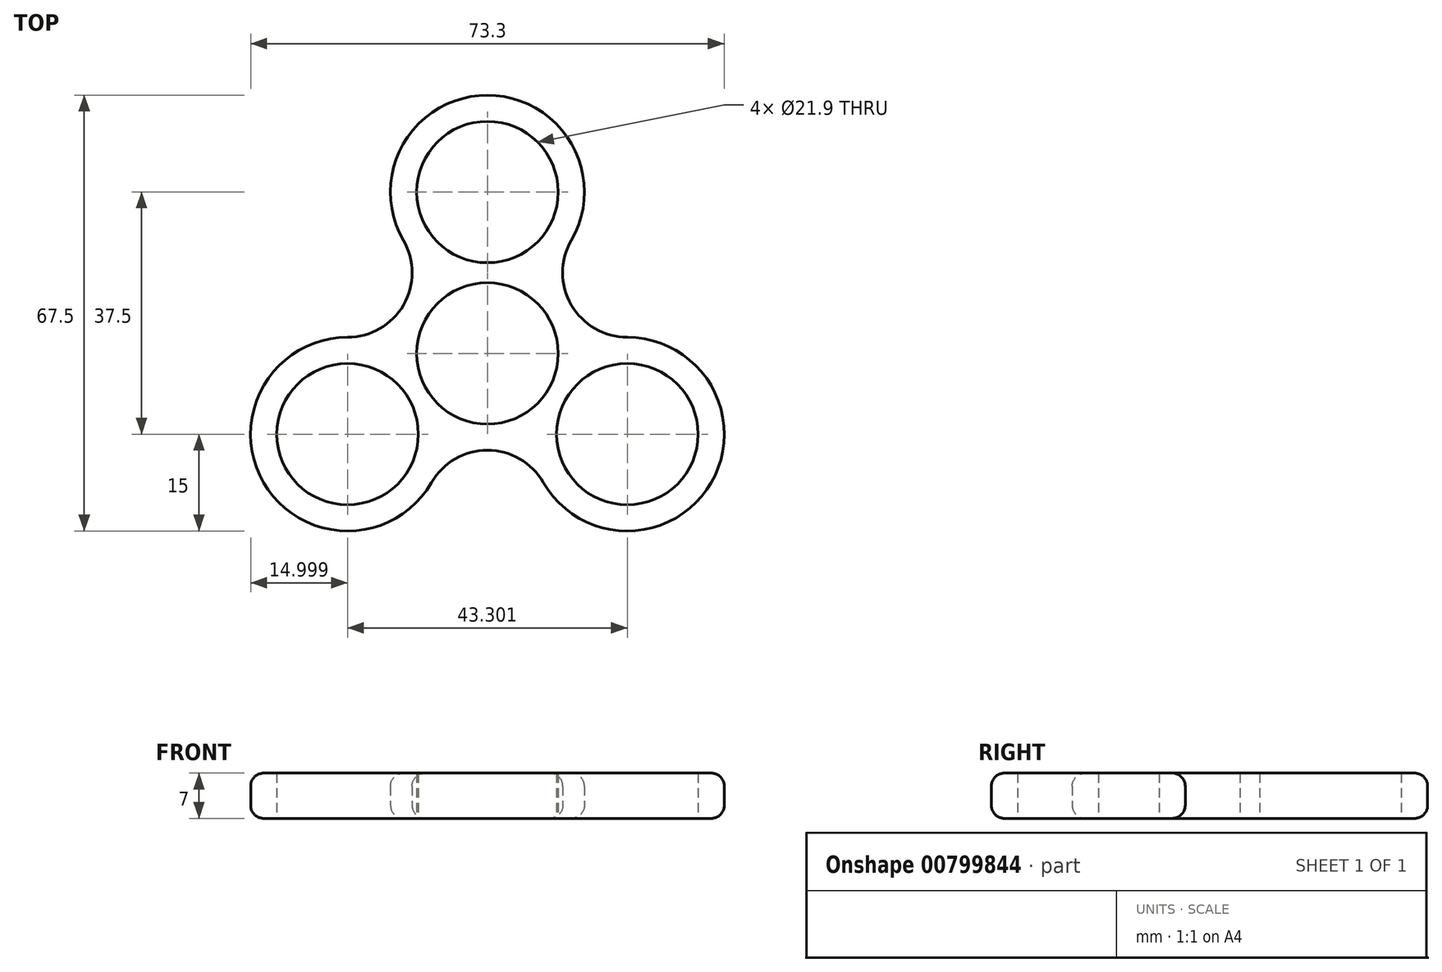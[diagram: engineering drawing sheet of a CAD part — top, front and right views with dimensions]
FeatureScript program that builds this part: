
annotation { "Feature Type Name" : "Feature", "Feature Type Description" : "" }
export const myFeature = defineFeature(function(context is Context, id is Id, definition is map)
    precondition{}
    {
        {
            var Q0;
            Q0=qCreatedBy(makeId("Top.planeOp"),FACE);
            var sketch = newSketch(context, id + "F0", { "sketchPlane" : qUnion([Q0])});
            skCircle(sketch, "E0", {"center": v(0, 0) * mm, "radius": 10.95 * mm});
            skCircle(sketch, "E1", {"center": v(0, 25) * mm, "radius": 10.95 * mm});
            skCircle(sketch, "E2", {"center": v(0, 0) * mm, "radius": 25 * mm});
            skCircle(sketch, "E3.1.0", {"center": v(-21.65, -12.5) * mm, "radius": 10.95 * mm});
            skCircle(sketch, "E3.2.0", {"center": v(21.65, -12.5) * mm, "radius": 10.95 * mm});
            skArc(sketch, "E4", {"start": v(13, 17.5) * mm, "mid": v(0, 40) * mm, "end": v(-13, 17.5) * mm});
            skArc(sketch, "E5.1.0", {"start": v(-21.65, 2.5) * mm, "mid": v(-34.64, -20) * mm, "end": v(-8.66, -20) * mm});
            skArc(sketch, "E5.2.0", {"start": v(8.66, -20) * mm, "mid": v(34.64, -20) * mm, "end": v(21.65, 2.5) * mm});
            skPoint(sketch, "E6.1.0", {"position": v(-21.65, 12.5) * mm});
            skPoint(sketch, "E6.3.0", {"position": v(0, -25) * mm});
            skPoint(sketch, "E6.5.0", {"position": v(21.65, 12.5) * mm});
            skArc(sketch, "E7", {"start": v(8.66, -20) * mm, "mid": v(0, -15) * mm, "end": v(-8.66, -20) * mm});
            skArc(sketch, "E8", {"start": v(-21.65, 2.5) * mm, "mid": v(-13, 7.5) * mm, "end": v(-13, 17.5) * mm});
            skArc(sketch, "E9.trimOffspring", {"start": v(13, 17.5) * mm, "mid": v(13, 7.5) * mm, "end": v(21.65, 2.5) * mm});
            skSolve(sketch);
        }
        {
            var Q0;
            {var subQ0=sQuery(id+"F0.wireOp",EDGE,"E2");var subQ1=sQuery(id+"F0.wireOp",EDGE,"E1");var subQ2=makeQuery(id+"F0.imprint","INTERSECT",VERTEX,{"disambiguationData":[OD(0.0)],"derivedFrom":[subQ1,subQ0]});Q0=makeQuery(id+"F0.imprint","IMPRINT",FACE,{"disambiguationData":[TD([[makeQuery(id+"F0.imprint","IMPRINT",EDGE,{"disambiguationData":[TD([[subQ2,-1.0]])],"derivedFrom":subQ1}),-1.0]])]});}
            var Q1;
            Q1=makeQuery(id+"F0.imprint","IMPRINT",FACE,{"disambiguationData":[TD([[makeQuery(id+"F0.imprint","IMPRINT",EDGE,{"derivedFrom":sQuery(id+"F0.wireOp",EDGE,"E0")}),-1.0]])]});
            var Q2;
            {var subQ0=sQuery(id+"F0.wireOp",EDGE,"E2");var subQ1=sQuery(id+"F0.wireOp",EDGE,"E3.1.0");var subQ2=makeQuery(id+"F0.imprint","INTERSECT",VERTEX,{"disambiguationData":[OD(0.0)],"derivedFrom":[subQ1,subQ0]});Q2=makeQuery(id+"F0.imprint","IMPRINT",FACE,{"disambiguationData":[TD([[makeQuery(id+"F0.imprint","IMPRINT",EDGE,{"disambiguationData":[TD([[subQ2,-1.0]])],"derivedFrom":subQ1}),-1.0]])]});}
            var Q3;
            {var subQ0=sQuery(id+"F0.wireOp",EDGE,"E2");var subQ1=sQuery(id+"F0.wireOp",EDGE,"E3.2.0");var subQ2=makeQuery(id+"F0.imprint","INTERSECT",VERTEX,{"disambiguationData":[OD(0.0)],"derivedFrom":[subQ1,subQ0]});Q3=makeQuery(id+"F0.imprint","IMPRINT",FACE,{"disambiguationData":[TD([[makeQuery(id+"F0.imprint","IMPRINT",EDGE,{"disambiguationData":[TD([[subQ2,-1.0]])],"derivedFrom":subQ1}),-1.0]])]});}
            extrude(context, id + "F1", {"entities" : qUnion([Q0, Q1, Q2, Q3]), "depth" : 7 * mm, "offsetDistance" : 25 * mm});
        }
        {
            var Q0;
            Q0=makeQuery(id+"F1.opExtrude","CAP_EDGE",EDGE,{"disambiguationData":[OSD([sQuery(id+"F0.wireOp",EDGE,"E5.1.0")])],"isStart":false});
            var Q1;
            Q1=makeQuery(id+"F1.opExtrude","CAP_EDGE",EDGE,{"disambiguationData":[OSD([sQuery(id+"F0.wireOp",EDGE,"E5.1.0")])],"isStart":true});
            fillet(context, id + "F2", {"entities" : qUnion([Q0, Q1]), "radius" : 2 * mm, "tangentPropagation" : true, "allowEdgeOverflow" : false});
        }
    });
